# Revit family: result
name_source: partatom
category: Plumbing Fixtures
revit_build: Autodesk Revit 2015 (Build: 20140903_1530(x64)
units: mm (PartAtom-declared; Revit-internal decimal feet)

## types (1)
- Default
    BIMobject category = Bath & Spas
    BIMobject category code = sanitary-bath-spas
    BIMobject main category = Sanitary
    BIMobject main category code = sanitary
    Brand url = http://www.duravit.com
    Edition number = 1
    GTIN code = https://4063382135124
    IFC Classification = Sanitary Terminal
    Manufacturer name = DURAVIT
    Masterformat 2014 Code = 22 41 19
    Masterformat 2014 Description = Residential Bathtubs
    NBS Reference Code = 35-06-08
    NBS Reference Description = Baths
    OmniClass Code = 23-31 15 17 11
    OmniClass Description = Bathtub Enclosures
    Product Guid = 116b5793-6482-4583-8a17-15408ba9abb8
    Product SKU = d-neo-bathtub-support-792427
    Product data url = https://bimobject.com
    Product family = D-Neo
    Product group = Bathtub support
    Product name = 792427 D-Neo Bathtub support
    Product url = https://duravit-public-assets.s3.eu-central-1.amazonaws.com
    QR code = http://bimobject.com
    UNSPSC Code = 30181501
    Uniclass 1.4 Code = L7211
    Uniclass 1.4 Description = Baths
    Uniclass 2.0 Code = PR-35-06-08
    Uniclass 2.0 Description = Baths
    Uniclass 2015 Code = Pr_40_20_06_08
    Uniclass 2015 Name = Baths
    Uniformat II Code = D2010
    Uniformat II Description = Plumbing Fixtures

## geometry (parser evidence)
native form markers: Sweep x3
no freeform markers — native parametric forms only
